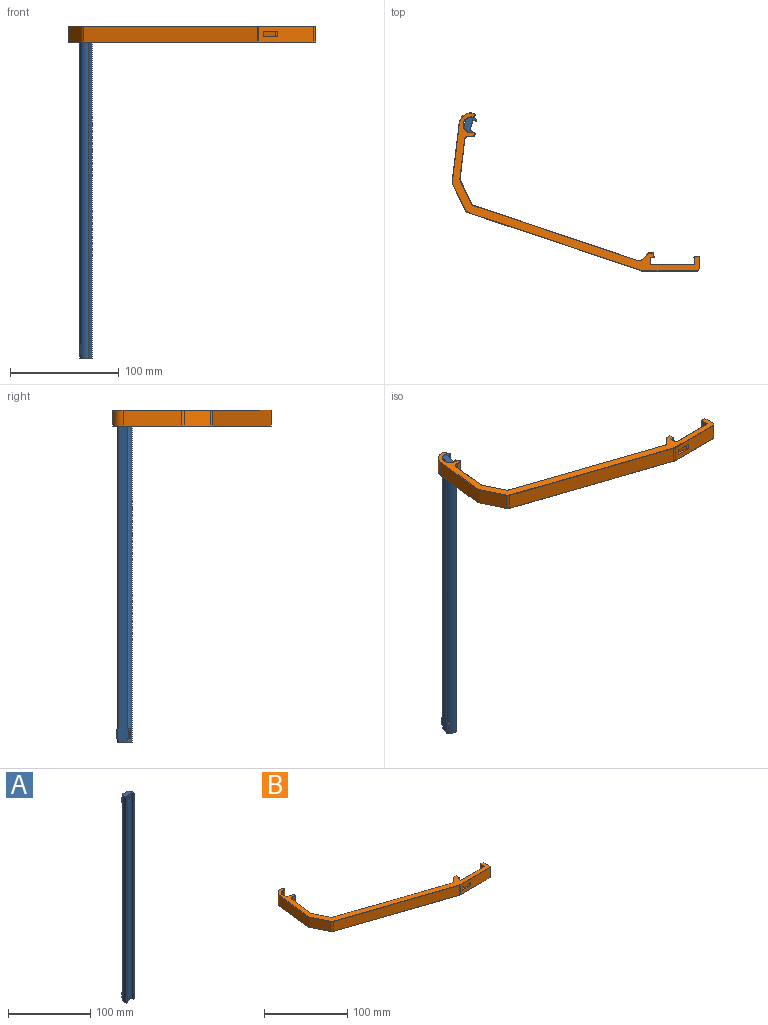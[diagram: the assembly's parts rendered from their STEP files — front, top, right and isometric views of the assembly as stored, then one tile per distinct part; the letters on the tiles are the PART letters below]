
ASSEMBLY  parts=2 mates=1
PART A: 50 faces, bbox 14.5x9.9x306 mm
  f0: plane 295.45x11.35mm, normal (0,1,0), area 2475.6mm2, adj f3,f5,f10,f12,f18,f19,f23,f24
  f1: plane 11.35x4.5mm, normal (0,1,0), area 40.4mm2, adj f3,f5,f10,f12,f21,f22,f29,f40
  f2: plane 305.95x10mm, normal (0,-1,0), area 3022.9mm2, adj f7,f8,f29,f30,f32,f33,f34,f35
  f3: cylinder r=8mm len=6.95mm, axis (0,0,-1), area 12.3mm2, adj f0,f1,f21,f27,f42,f44,f46,f49
  f4: plane 8.95x0.67mm, normal (-0.43,-0.9,0), area 6.1mm2, adj f5,f21,f27,f49
  f5: cylinder r=7mm len=305.95mm, axis (0,0,-1), area 3039.7mm2, adj f0,f1,f4,f6,f16,f21,f25,f26
  f6: plane 305.95x1.1mm, normal (0,-1,0), area 337.5mm2, adj f5,f7,f29,f30
  f7: plane 305.95x3mm, normal (1,0,0), area 917.9mm2, adj f2,f6,f29,f30
  f8: plane 305.95x3mm, normal (-1,0,0), area 917.9mm2, adj f2,f9,f29,f30
  f9: plane 305.95x1.1mm, normal (0,-1,0), area 337.5mm2, adj f8,f10,f29,f30
  f10: cylinder r=7mm len=305.95mm, axis (0,0,-1), area 3039.7mm2, adj f0,f1,f9,f11,f13,f22,f23,f24
  f11: plane 8.95x0.67mm, normal (0.43,-0.9,0), area 6.1mm2, adj f10,f22,f28,f48
  f12: cylinder r=8mm len=6.95mm, axis (0,0,-1), area 12.3mm2, adj f0,f1,f22,f28,f39,f41,f43,f48
  f13: plane 9x0.44mm, normal (0.43,-0.9,0), area 4.1mm2, adj f10,f17,f23,f24
  f14: cylinder r=8mm len=7mm, axis (0,0,1), area 13.8mm2, adj f17,f18,f23,f24
  f15: cylinder r=8mm len=7mm, axis (0,0,1), area 13.8mm2, adj f19,f20,f25,f26
  f16: plane 9x0.44mm, normal (-0.43,-0.9,0), area 4.1mm2, adj f5,f20,f25,f26
  f17: cylinder r=0.5mm len=8.03mm, axis (0,0,1), area 6mm2, adj f13,f14,f23,f24
  f18: cylinder r=0.5mm len=7.3mm, axis (0,0,1), area 2.9mm2, adj f0,f14,f23,f24
  f19: cylinder r=0.5mm len=7.3mm, axis (0,0,1), area 2.9mm2, adj f0,f15,f25,f26
  f20: cylinder r=0.5mm len=8.03mm, axis (0,0,1), area 6mm2, adj f15,f16,f25,f26
  f21: cone r=7mm half-angle=45deg, axis (0,0,-1), area 4.3mm2, adj f1,f3,f4,f5,f49
  f22: cone r=7mm half-angle=45deg, axis (0,0,-1), area 4.3mm2, adj f1,f10,f11,f12,f48
  f23: cone r=8mm half-angle=45deg, axis (0,0,1), area 4.3mm2, adj f0,f10,f13,f14,f17,f18
  f24: cone r=7mm half-angle=45deg, axis (0,0,-1), area 4.3mm2, adj f0,f10,f13,f14,f17,f18
  f25: cone r=7mm half-angle=45deg, axis (0,0,-1), area 4.3mm2, adj f0,f5,f15,f16,f19,f20
  f26: cone r=8mm half-angle=45deg, axis (0,0,1), area 4.3mm2, adj f0,f5,f15,f16,f19,f20
  f27: cone r=8mm half-angle=45deg, axis (0,0,1), area 4.3mm2, adj f0,f3,f4,f5,f49
  f28: cone r=8mm half-angle=45deg, axis (0,0,1), area 4.3mm2, adj f0,f10,f11,f12,f48
  f29: plane 14x9.07mm, normal (0,0,1), area 85.3mm2, adj f1,f2,f5,f6,f7,f8,f9,f10
  f30: plane 14x9.07mm, normal (0,0,-1), area 85.3mm2, adj f0,f2,f5,f6,f7,f8,f9,f10
  f31: plane 10.99x1.57mm, normal (0,0,-1), area 14.9mm2, adj f35,f36,f37,f39,f40,f41,f42,f44
  f32: plane 9x1.86mm, normal (-1,0,0), area 15mm2, adj f2,f33,f35,f47
  f33: plane 10.99x5.57mm, normal (0,0,1), area 34.9mm2, adj f2,f32,f34,f36,f37,f38,f41,f43
  f34: plane 9x1.86mm, normal (1,0,0), area 15mm2, adj f2,f33,f35,f38
  f35: plane 7.93x4mm, normal (0,-0.71,-0.71), area 28.3mm2, adj f2,f31,f32,f34,f36,f37,f38,f47
  f36: plane 6.79x3.29mm, normal (-0.71,0.71,0), area 25.5mm2, adj f31,f33,f35,f41,f47
  f37: plane 6.79x3.29mm, normal (0.71,0.71,0), area 25.5mm2, adj f31,f33,f35,f38,f44
  f38: cylinder r=0.5mm len=7.14mm, axis (0,0,-1), area 2.7mm2, adj f33,f34,f35,f37
  f39: torus R=7.5mm, axis (0,0,-1), area 0.3mm2, adj f12,f31,f40,f41
  f40: cylinder r=0.5mm len=11.35mm, axis (-1,0,0), area 8.8mm2, adj f1,f31,f39,f42
  f41: cylinder r=0.5mm len=6mm, axis (0,0,-1), area 4.5mm2, adj f12,f31,f33,f36,f39,f43
  f42: torus R=7.5mm, axis (0,0,-1), area 0.3mm2, adj f3,f31,f40,f44
  f43: torus R=7.5mm, axis (0,0,-1), area 0.3mm2, adj f12,f33,f41,f45
  f44: cylinder r=0.5mm len=6mm, axis (0,0,-1), area 4.5mm2, adj f3,f31,f33,f37,f42,f46
  f45: cylinder r=0.5mm len=11.35mm, axis (1,0,0), area 8.8mm2, adj f0,f33,f43,f46
  f46: torus R=7.5mm, axis (0,0,-1), area 0.3mm2, adj f3,f33,f44,f45
  f47: cylinder r=0.5mm len=7.14mm, axis (0,0,1), area 2.7mm2, adj f32,f33,f35,f36
  f48: plane 7.46x0.35mm, normal (0.95,-0.32,0), area 2.6mm2, adj f11,f12,f22,f28
  f49: plane 7.46x0.35mm, normal (-0.95,-0.32,0), area 2.6mm2, adj f3,f4,f21,f27
PART B: 116 faces, bbox 228.3x145.8x15 mm
  f0: cylinder r=11mm len=14.5mm, axis (0,0,-1), area 260.9mm2, adj f1,f22,f70,f101
  f1: plane 54.05x14.5mm, normal (-0.99,0.12,0), area 789.2mm2, adj f0,f39,f72,f103
  f2: plane 24.09x14.5mm, normal (-0.9,-0.44,0), area 388.8mm2, adj f39,f40,f76,f107
  f3: plane 159.92x53.73mm, normal (-0.32,-0.95,0), area 2446.3mm2, adj f40,f41,f80,f111
  f4: plane 50.6x14.5mm, normal (0,-1,0), area 667.2mm2, adj f28,f29,f41,f45,f50,f53,f84,f115
  f5: plane 14.5x11.7mm, normal (1,0,0), area 169.6mm2, adj f6,f53,f81,f112
  f6: plane 14.5x5mm, normal (0,1,0), area 72.5mm2, adj f5,f7,f79,f110
  f7: plane 14.5x0.75mm, normal (-0.71,0.71,0), area 15.4mm2, adj f6,f8,f77,f108
  f8: plane 14.5x0.75mm, normal (-0.71,-0.71,0), area 15.4mm2, adj f7,f9,f75,f106
  f9: plane 14.5x6.2mm, normal (-1,0,0), area 89.9mm2, adj f8,f10,f73,f104
  f10: plane 40.25x14.5mm, normal (0,1,0), area 583.6mm2, adj f9,f11,f71,f102
  f11: plane 14.5x6.2mm, normal (1,0,0), area 89.9mm2, adj f10,f12,f69,f100
  f12: plane 14.5x3mm, normal (0.02,-1,0), area 43.5mm2, adj f11,f13,f67,f98
  f13: plane 14.5x4.64mm, normal (1,0.02,0), area 67.3mm2, adj f12,f14,f65,f96
  f14: plane 14.5x5mm, normal (0,1,0), area 72.5mm2, adj f13,f15,f63,f94
  f15: plane 14.5x6mm, normal (-0.71,0.71,0), area 123mm2, adj f14,f42,f61,f92
  f16: plane 150.58x50.59mm, normal (0.32,0.95,0), area 2303.4mm2, adj f42,f43,f57,f88
  f17: plane 20.63x14.5mm, normal (0.9,0.44,0), area 333mm2, adj f43,f44,f54,f85
  f18: plane 35.04x14.5mm, normal (0.99,-0.12,0), area 511.7mm2, adj f38,f44,f58,f89
  f19: cylinder r=11mm len=14.5mm, axis (0,0,-1), area 51.2mm2, adj f20,f38,f62,f93
  f20: cylinder r=2mm len=14.5mm, axis (0,0,-1), area 91.1mm2, adj f19,f21,f64,f95
  f21: cylinder r=7mm len=14.5mm, axis (0,0,-1), area 162.2mm2, adj f20,f22,f27,f32,f51,f52,f66,f97
  f22: cylinder r=2mm len=14.5mm, axis (0,0,-1), area 91.1mm2, adj f0,f21,f68,f99
  f23: plane 227.8x145.32mm, normal (0,0,1), area 2302.6mm2, adj f85,f86,f87,f88,f89,f90,f91,f92
  f24: plane 227.8x145.32mm, normal (0,0,-1), area 2302.6mm2, adj f54,f55,f56,f57,f58,f59,f60,f61
  f25: plane 162.94x54.73mm, normal (0.32,0.95,0), area 859.4mm2, adj f28,f29,f47,f50
  f26: plane 172.36x57.89mm, normal (-0.32,-0.95,0), area 909.1mm2, adj f28,f29,f45,f48
  f27: plane 9x2mm, normal (-1,0,0), area 14mm2, adj f21,f31,f51,f52
  f28: plane 190.84x134.82mm, normal (0,0,-1), area 773.6mm2, adj f4,f25,f26,f30,f34,f35,f36,f37
  f29: plane 190.84x134.82mm, normal (0,0,1), area 773.6mm2, adj f4,f25,f26,f30,f34,f35,f36,f37
  f30: plane 44.52x5.29mm, normal (-0.99,0.12,0), area 224.2mm2, adj f28,f29,f31,f49
  f31: cylinder r=9mm len=6.62mm, axis (0,0,-1), area 37.2mm2, adj f27,f30,f51,f52
  f32: plane 9x2mm, normal (-1,0,0), area 14mm2, adj f21,f33,f51,f52
  f33: cylinder r=9mm len=9mm, axis (0,0,-1), area 70.7mm2, adj f32,f34,f51,f52
  f34: plane 8.9x5mm, normal (0.99,-0.11,0), area 44.8mm2, adj f28,f29,f33,f35
  f35: plane 42.26x5.02mm, normal (0.99,-0.12,0), area 212.8mm2, adj f28,f29,f34,f46
  f36: plane 22.63x11.36mm, normal (0.89,0.45,0), area 126.6mm2, adj f28,f29,f46,f47
  f37: plane 20.72x10.4mm, normal (-0.89,-0.45,0), area 115.9mm2, adj f28,f29,f48,f49
  f38: cylinder r=4mm len=14.5mm, axis (0,0,-1), area 91.1mm2, adj f18,f19,f60,f91
  f39: cylinder r=4mm len=14.5mm, axis (0,0,-1), area 33.2mm2, adj f1,f2,f74,f105
  f40: cylinder r=4mm len=14.5mm, axis (0,0,-1), area 45.9mm2, adj f2,f3,f78,f109
  f41: cylinder r=4mm len=14.5mm, axis (0,0,-1), area 18.8mm2, adj f3,f4,f82,f113
  f42: cylinder r=4mm len=14.5mm, axis (0,0,1), area 65.7mm2, adj f15,f16,f59,f90
  f43: cylinder r=4mm len=14.5mm, axis (0,0,1), area 45.9mm2, adj f16,f17,f55,f86
  f44: cylinder r=4mm len=14.5mm, axis (0,0,1), area 33.2mm2, adj f17,f18,f56,f87
  f45: cylinder r=5mm len=5mm, axis (0,0,-1), area 8.1mm2, adj f4,f26,f28,f29
  f46: cylinder r=5mm len=5mm, axis (0,0,1), area 14.6mm2, adj f28,f29,f35,f36
  f47: cylinder r=5mm len=5mm, axis (0,0,1), area 19.5mm2, adj f25,f28,f29,f36
  f48: cylinder r=5mm len=5mm, axis (0,0,-1), area 19.5mm2, adj f26,f28,f29,f37
  f49: cylinder r=5mm len=5mm, axis (0,0,-1), area 14.6mm2, adj f28,f29,f30,f37
  f50: cylinder r=0.5mm len=5mm, axis (0,0,1), area 7mm2, adj f4,f25,f28,f29
  f51: cone r=7mm half-angle=45deg, axis (0,0,1), area 71.1mm2, adj f21,f27,f29,f31,f32,f33
  f52: cone r=9mm half-angle=45deg, axis (0,0,-1), area 71.1mm2, adj f21,f27,f28,f31,f32,f33
  f53: plane 14.5x2mm, normal (0.71,-0.71,0), area 41mm2, adj f4,f5,f83,f114
  f54: plane 20.74x10.31mm, normal (0.64,0.31,-0.71), area 8.1mm2, adj f17,f24,f55,f56
  f55: cone r=4.25mm half-angle=45deg, axis (0,0,-1), area 1.2mm2, adj f24,f43,f54,f57
  f56: cone r=4.25mm half-angle=45deg, axis (0,0,-1), area 0.8mm2, adj f24,f44,f54,f58
  f57: plane 150.66x50.83mm, normal (0.23,0.67,-0.71), area 56.2mm2, adj f16,f24,f55,f59
  f58: plane 35.07x4.39mm, normal (0.7,-0.08,-0.71), area 12.5mm2, adj f18,f24,f56,f60
  f59: cone r=4.25mm half-angle=45deg, axis (0,0,-1), area 1.7mm2, adj f24,f42,f57,f61
  f60: cone r=4.25mm half-angle=45deg, axis (0,0,-1), area 2.3mm2, adj f24,f38,f58,f62
  f61: plane 6.18x6.1mm, normal (-0.5,0.5,-0.71), area 3mm2, adj f15,f24,f59,f63
  f62: cone r=11mm half-angle=45deg, axis (0,0,1), area 1.2mm2, adj f19,f24,f60,f64
  f63: plane 5x0.25mm, normal (0,0.71,-0.71), area 1.7mm2, adj f14,f24,f61,f65
  f64: cone r=2mm half-angle=45deg, axis (0,0,1), area 2.1mm2, adj f20,f24,f62,f66
  f65: plane 4.64x0.33mm, normal (0.71,0.01,-0.71), area 1.6mm2, adj f13,f24,f63,f67
  f66: cone r=7.25mm half-angle=45deg, axis (0,0,-1), area 8.9mm2, adj f21,f24,f64,f68
  f67: plane 3.25x0.3mm, normal (0.01,-0.71,-0.71), area 1.1mm2, adj f12,f24,f65,f69
  f68: cone r=2mm half-angle=45deg, axis (0,0,1), area 2.1mm2, adj f22,f24,f66,f70
  f69: plane 6.7x0.25mm, normal (0.71,0,-0.71), area 2.3mm2, adj f11,f24,f67,f71
  f70: cone r=11mm half-angle=45deg, axis (0,0,1), area 6.3mm2, adj f0,f24,f68,f72
  f71: plane 40.75x0.25mm, normal (0,0.71,-0.71), area 14.3mm2, adj f10,f24,f69,f73
  f72: plane 54.08x6.63mm, normal (-0.7,0.08,-0.71), area 19.2mm2, adj f1,f24,f70,f74
  f73: plane 6.55x0.25mm, normal (-0.71,0,-0.71), area 2.3mm2, adj f9,f24,f71,f75
  f74: cone r=3.75mm half-angle=45deg, axis (0,0,1), area 0.8mm2, adj f24,f39,f72,f76
  f75: plane 1x0.75mm, normal (-0.5,-0.5,-0.71), area 0.3mm2, adj f8,f24,f73,f77
  f76: plane 24.2x12mm, normal (-0.64,-0.31,-0.71), area 9.5mm2, adj f2,f24,f74,f78
  f77: plane 0.85x0.75mm, normal (-0.5,0.5,-0.71), area 0.3mm2, adj f7,f24,f75,f79
  f78: cone r=3.75mm half-angle=45deg, axis (0,0,1), area 1.1mm2, adj f24,f40,f76,f80
  f79: plane 5x0.25mm, normal (0,0.71,-0.71), area 1.7mm2, adj f6,f24,f77,f81
  f80: plane 160x53.96mm, normal (-0.23,-0.67,-0.71), area 59.6mm2, adj f3,f24,f78,f82
  f81: plane 11.7x0.25mm, normal (0.71,0,-0.71), area 4.1mm2, adj f5,f24,f79,f83
  f82: cone r=3.75mm half-angle=45deg, axis (0,0,1), area 0.4mm2, adj f24,f41,f80,f84
  f83: plane 2.1x2.1mm, normal (0.5,-0.5,-0.71), area 1mm2, adj f24,f53,f81,f84
  f84: plane 50.6x0.25mm, normal (0,-0.71,-0.71), area 17.9mm2, adj f4,f24,f82,f83
  f85: plane 20.74x10.31mm, normal (0.64,0.31,0.71), area 8.1mm2, adj f17,f23,f86,f87
  f86: cone r=4.25mm half-angle=45deg, axis (0,0,1), area 1.2mm2, adj f23,f43,f85,f88
  f87: cone r=4.25mm half-angle=45deg, axis (0,0,1), area 0.8mm2, adj f23,f44,f85,f89
  f88: plane 150.66x50.83mm, normal (0.23,0.67,0.71), area 56.2mm2, adj f16,f23,f86,f90
  f89: plane 35.07x4.39mm, normal (0.7,-0.08,0.71), area 12.5mm2, adj f18,f23,f87,f91
  f90: cone r=4.25mm half-angle=45deg, axis (0,0,1), area 1.7mm2, adj f23,f42,f88,f92
  f91: cone r=4.25mm half-angle=45deg, axis (0,0,1), area 2.3mm2, adj f23,f38,f89,f93
  f92: plane 6.18x6.1mm, normal (-0.5,0.5,0.71), area 3mm2, adj f15,f23,f90,f94
  f93: cone r=10.75mm half-angle=45deg, axis (0,0,-1), area 1.2mm2, adj f19,f23,f91,f95
  f94: plane 5x0.25mm, normal (0,0.71,0.71), area 1.7mm2, adj f14,f23,f92,f96
  f95: cone r=1.75mm half-angle=45deg, axis (0,0,-1), area 2.1mm2, adj f20,f23,f93,f97
  f96: plane 4.64x0.33mm, normal (0.71,0.01,0.71), area 1.6mm2, adj f13,f23,f94,f98
  f97: cone r=7mm half-angle=45deg, axis (0,0,1), area 8.9mm2, adj f21,f23,f95,f99
  f98: plane 3.25x0.3mm, normal (0.01,-0.71,0.71), area 1.1mm2, adj f12,f23,f96,f100
  f99: cone r=1.75mm half-angle=45deg, axis (0,0,-1), area 2.1mm2, adj f22,f23,f97,f101
  f100: plane 6.7x0.25mm, normal (0.71,0,0.71), area 2.3mm2, adj f11,f23,f98,f102
  f101: cone r=10.75mm half-angle=45deg, axis (0,0,-1), area 6.3mm2, adj f0,f23,f99,f103
  f102: plane 40.75x0.25mm, normal (0,0.71,0.71), area 14.3mm2, adj f10,f23,f100,f104
  f103: plane 54.08x6.63mm, normal (-0.7,0.08,0.71), area 19.2mm2, adj f1,f23,f101,f105
  f104: plane 6.55x0.25mm, normal (-0.71,0,0.71), area 2.3mm2, adj f9,f23,f102,f106
  f105: cone r=3.75mm half-angle=45deg, axis (0,0,-1), area 0.8mm2, adj f23,f39,f103,f107
  f106: plane 1x0.75mm, normal (-0.5,-0.5,0.71), area 0.3mm2, adj f8,f23,f104,f108
  f107: plane 24.2x12mm, normal (-0.64,-0.31,0.71), area 9.5mm2, adj f2,f23,f105,f109
  f108: plane 0.85x0.75mm, normal (-0.5,0.5,0.71), area 0.3mm2, adj f7,f23,f106,f110
  f109: cone r=3.75mm half-angle=45deg, axis (0,0,-1), area 1.1mm2, adj f23,f40,f107,f111
  f110: plane 5x0.25mm, normal (0,0.71,0.71), area 1.7mm2, adj f6,f23,f108,f112
  f111: plane 160x53.96mm, normal (-0.23,-0.67,0.71), area 59.6mm2, adj f3,f23,f109,f113
  f112: plane 11.7x0.25mm, normal (0.71,0,0.71), area 4.1mm2, adj f5,f23,f110,f114
  f113: cone r=3.75mm half-angle=45deg, axis (0,0,-1), area 0.4mm2, adj f23,f41,f111,f115
  f114: plane 2.1x2.1mm, normal (0.5,-0.5,0.71), area 1mm2, adj f23,f53,f112,f115
  f115: plane 50.6x0.25mm, normal (0,-0.71,0.71), area 17.9mm2, adj f4,f23,f113,f114
PLACE A rot(axis=(0,0,1),72.5deg) t=(-41.97,75.69,8.84)mm
PLACE B t=(18.24,-36.4,5.79)mm fixed
MATE revolute A.f3 <-> B.f0  axis (0,0,1) through (-99.85,69.04,20.79)mm
